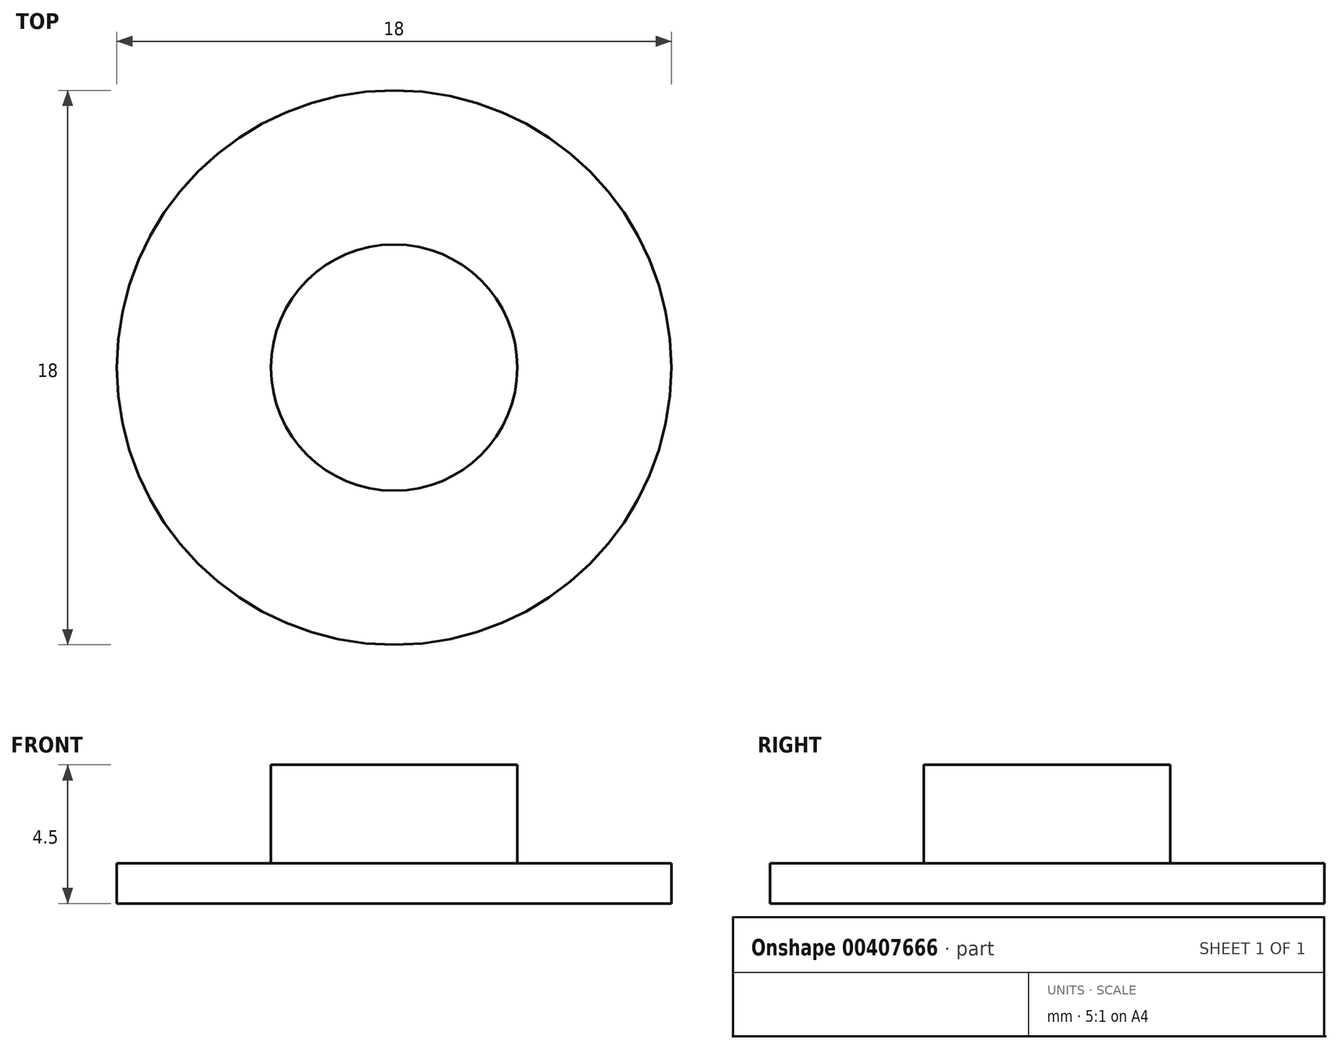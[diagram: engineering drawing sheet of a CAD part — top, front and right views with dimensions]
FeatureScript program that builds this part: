
annotation { "Feature Type Name" : "Feature", "Feature Type Description" : "" }
export const myFeature = defineFeature(function(context is Context, id is Id, definition is map)
    precondition{}
    {
        {
            var Q0;
            Q0=qCreatedBy(makeId("Top.planeOp"),FACE);
            var sketch = newSketch(context, id + "F0", { "sketchPlane" : qUnion([Q0])});
            skCircle(sketch, "E0", {"center": v(0, 0) * mm, "radius": 9 * mm});
            skSolve(sketch);
        }
        {
            var Q0;
            Q0=qSketchRegion(id+"F0",true);
            extrude(context, id + "F1", {"entities" : qUnion([Q0]), "depth" : 1.3 * mm});
        }
        {
            var Q0;
            Q0=makeQuery(id+"F1.opExtrude","CAP_FACE",FACE,{"disambiguationData":[OSD([sQuery(id+"F0.wireOp",EDGE,"E0")])],"isStart":false});
            var sketch = newSketch(context, id + "F2", { "sketchPlane" : qUnion([Q0])});
            skCircle(sketch, "E1", {"center": v(0, 0) * mm, "radius": 4 * mm});
            skSolve(sketch);
        }
        {
            var Q0;
            Q0=makeQuery(id+"F2.imprint","IMPRINT",FACE,{"disambiguationData":[TD([[makeQuery(id+"F2.imprint","IMPRINT",EDGE,{"derivedFrom":sQuery(id+"F2.wireOp",EDGE,"E1")}),1.0]])]});
            extrude(context, id + "F3", {"entities" : qUnion([Q0]), "operationType" : NewBodyOperationType.ADD, "depth" : 3.2 * mm, "offsetDistance" : 25 * mm});
        }
    });
